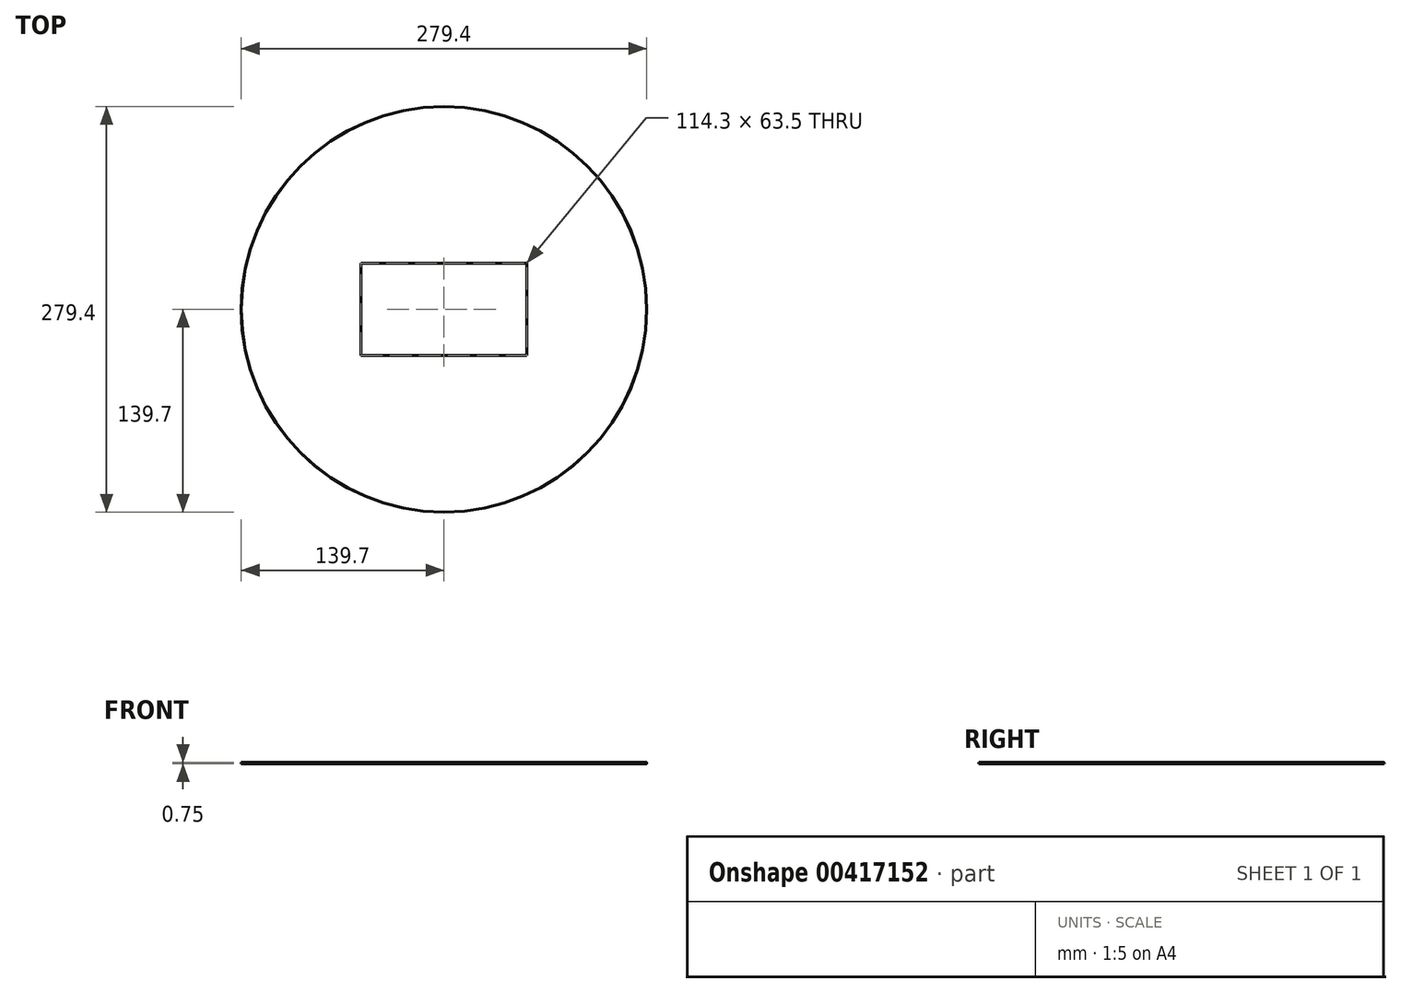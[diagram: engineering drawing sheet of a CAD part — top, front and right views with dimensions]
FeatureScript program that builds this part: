
annotation { "Feature Type Name" : "Feature", "Feature Type Description" : "" }
export const myFeature = defineFeature(function(context is Context, id is Id, definition is map)
    precondition{}
    {
        {
            assignVariable(context, id + "F0", {"name" : "BaseThickness", "anyValue" : 0.75});
        }
        {
            assignVariable(context, id + "F1", {"name" : "OuterChamfer", "anyValue" : 0.06});
        }
        {
            var Q0;
            Q0=qCreatedBy(makeId("Top.planeOp"),FACE);
            var sketch = newSketch(context, id + "F2", { "sketchPlane" : qUnion([Q0])});
            skCircle(sketch, "E0", {"center": v(0, 0) * mm, "radius": 139.7 * mm});
            skCircle(sketch, "E1", {"center": v(0, 0) * mm, "radius": 2.98 * mm});
            skSolve(sketch);
        }
        {
            var Q0;
            Q0=qSketchRegion(id+"F2",true);
            extrude(context, id + "F3", {"entities" : qUnion([Q0]), "depth" : (getVariable(context, 'BaseThickness')) * mm});
        }
        {
            var Q0;
            Q0=makeQuery(id+"F3.opExtrude","CAP_EDGE",EDGE,{"disambiguationData":[OSD([sQuery(id+"F2.wireOp",EDGE,"E0")])],"isStart":false});
            var Q1;
            Q1=makeQuery(id+"F3.opExtrude","CAP_EDGE",EDGE,{"disambiguationData":[OSD([sQuery(id+"F2.wireOp",EDGE,"E0")])],"isStart":true});
            chamfer(context, id + "F4", {"entities" : qUnion([Q0, Q1]), "width" : (getVariable(context, 'OuterChamfer')) * mm, "tangentPropagation" : true});
        }
        {
            var Q0;
            Q0=qCreatedBy(makeId("Front.planeOp"),FACE);
            cPlane(context, id + "F5", {"entities" : qUnion([Q0]), "cplaneType" : CPlaneType.OFFSET, "offset" : (5.5 * 25.4) * mm, "width" : 150 * mm, "height" : 150 * mm});
        }
        {
            var Q0;
            Q0=qCreatedBy(id+"F5.planeOp",FACE);
            var sketch = newSketch(context, id + "F6", { "sketchPlane" : qUnion([Q0])});
            skLineSegment(sketch, "E2", {"start": v(-143.85, 0) * mm, "end": v(140.68, 0) * mm, "construction": true});
            skLineSegment(sketch, "E3", {"start": v(-145.32, 19.05) * mm, "end": v(140.92, 19.05) * mm, "construction": true});
            skLineSegment(sketch, "E4.bottom", {"start": v(-6.35, 19.05) * mm, "end": v(6.35, 19.05) * mm});
            skLineSegment(sketch, "E4.top", {"start": v(-6.35, 13.5) * mm, "end": v(6.35, 13.5) * mm});
            skLineSegment(sketch, "E4.left", {"start": v(-6.35, 19.05) * mm, "end": v(-6.35, 13.5) * mm});
            skLineSegment(sketch, "E4.right", {"start": v(6.35, 19.05) * mm, "end": v(6.35, 13.5) * mm});
            skSolve(sketch);
        }
        {
            var Q0;
            Q0=makeQuery(id+"F6.imprint","IMPRINT",FACE,{"disambiguationData":[TD([[makeQuery(id+"F6.imprint","IMPRINT",EDGE,{"derivedFrom":sQuery(id+"F6.wireOp",EDGE,"E4.bottom")}),-1.0]])]});
            extrude(context, id + "F7", {"entities" : qUnion([Q0]), "operationType" : NewBodyOperationType.REMOVE, "oppositeDirection" : true, "depth" : 38.1 * mm});
        }
        {
            var Q0;
            Q0=makeQuery(id+"F3.opExtrude","CAP_FACE",FACE,{"disambiguationData":[OSD([sQuery(id+"F2.wireOp",EDGE,"E0"),sQuery(id+"F2.wireOp",EDGE,"E1")])],"isStart":false});
            var sketch = newSketch(context, id + "F8", { "sketchPlane" : qUnion([Q0])});
            skLineSegment(sketch, "E5.bottom", {"start": v(-57.15, 31.75) * mm, "end": v(57.15, 31.75) * mm});
            skLineSegment(sketch, "E5.top", {"start": v(-57.15, -31.75) * mm, "end": v(57.15, -31.75) * mm});
            skLineSegment(sketch, "E5.left", {"start": v(-57.15, 31.75) * mm, "end": v(-57.15, -31.75) * mm});
            skLineSegment(sketch, "E5.right", {"start": v(57.15, 31.75) * mm, "end": v(57.15, -31.75) * mm});
            skSolve(sketch);
        }
        {
            var Q0;
            Q0=makeQuery(id+"F8.imprint","IMPRINT",FACE,{"disambiguationData":[TD([[makeQuery(id+"F8.imprint","IMPRINT",EDGE,{"derivedFrom":sQuery(id+"F8.wireOp",EDGE,"E5.bottom")}),-1.0]])]});
            extrude(context, id + "F9", {"entities" : qUnion([Q0]), "operationType" : NewBodyOperationType.REMOVE, "endBound" : BoundingType.THROUGH_ALL, "oppositeDirection" : true, "depth" : 25.4 * mm});
        }
    });
